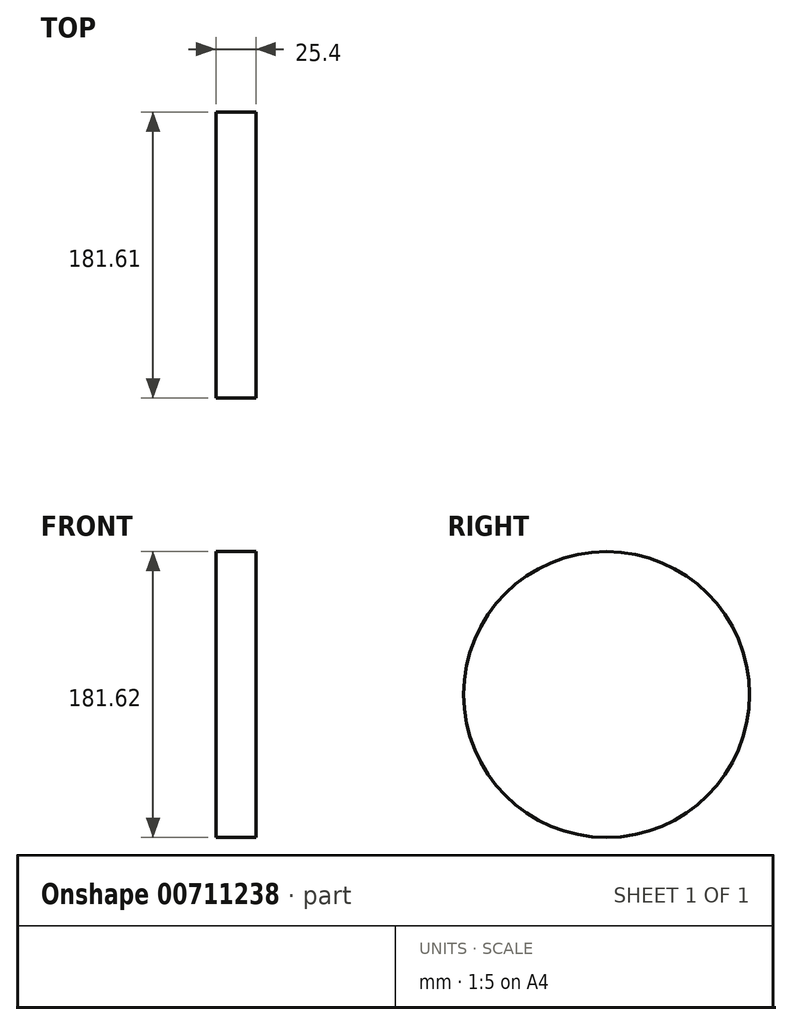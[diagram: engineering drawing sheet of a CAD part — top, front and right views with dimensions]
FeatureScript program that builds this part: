
annotation { "Feature Type Name" : "Feature", "Feature Type Description" : "" }
export const myFeature = defineFeature(function(context is Context, id is Id, definition is map)
    precondition{}
    {
        {
            var Q0;
            Q0=qCreatedBy(makeId("Right.planeOp"),FACE);
            var sketch = newSketch(context, id + "F0", { "sketchPlane" : qUnion([Q0])});
            skCircle(sketch, "E0", {"center": v(90.8, 0) * mm, "radius": 90.8 * mm});
            skSolve(sketch);
        }
        {
            var Q0;
            Q0=makeQuery(id+"F0.imprint","IMPRINT",FACE,{"disambiguationData":[TD([[makeQuery(id+"F0.imprint","IMPRINT",EDGE,{"derivedFrom":sQuery(id+"F0.wireOp",EDGE,"E0")}),1.0]])]});
            extrude(context, id + "F1", {"entities" : qUnion([Q0]), "depth" : 25.4 * mm, "offsetDistance" : 25.4 * mm});
        }
    });
